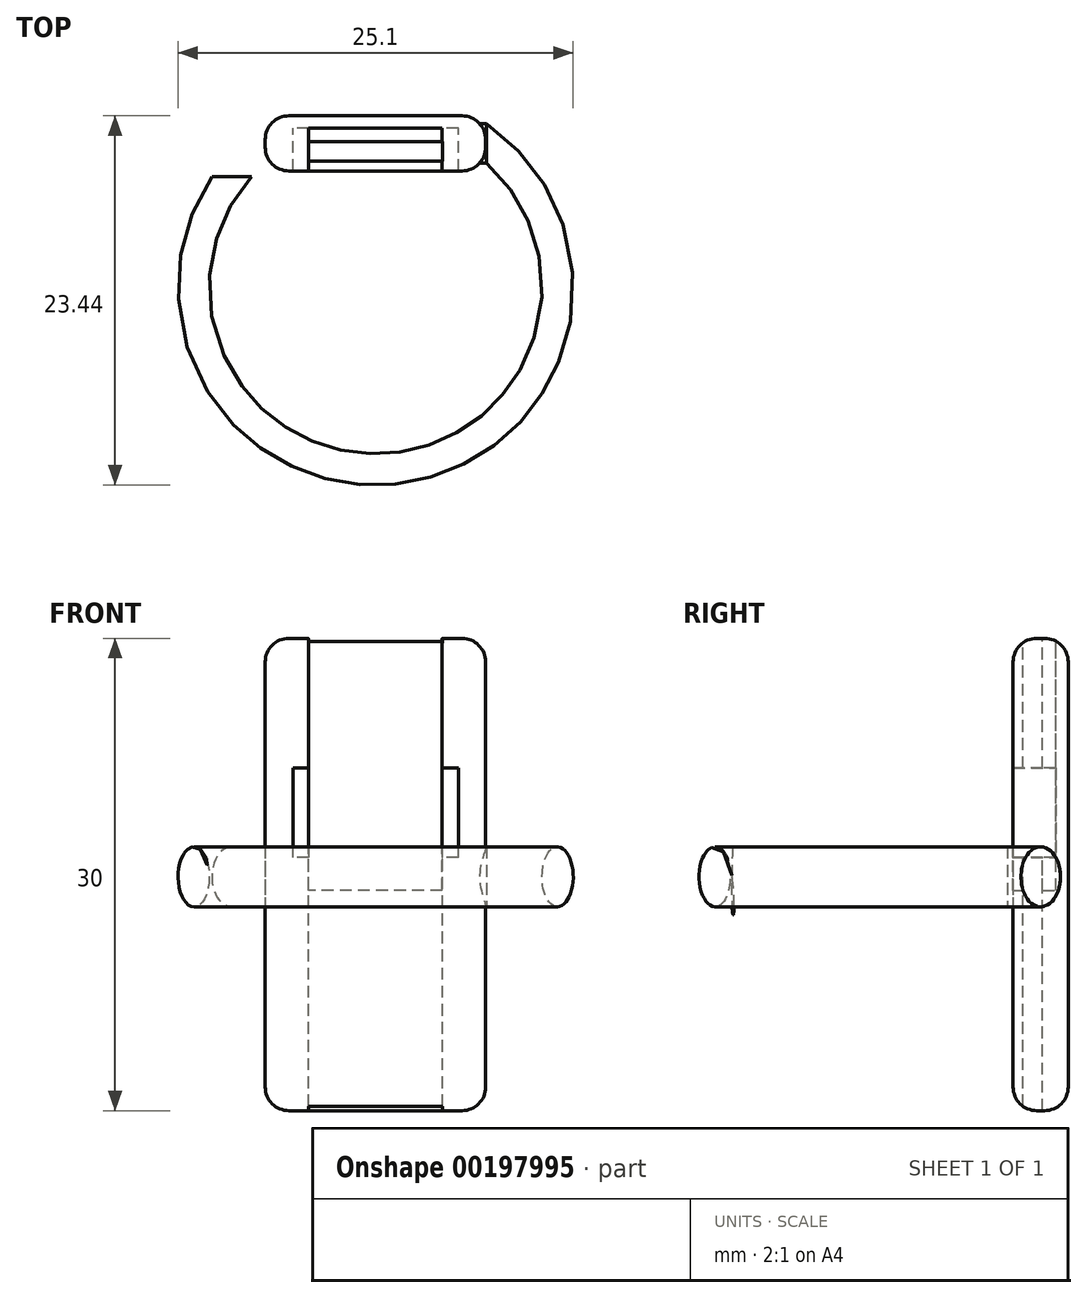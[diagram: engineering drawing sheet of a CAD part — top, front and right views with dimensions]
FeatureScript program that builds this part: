
annotation { "Feature Type Name" : "Feature", "Feature Type Description" : "" }
export const myFeature = defineFeature(function(context is Context, id is Id, definition is map)
    precondition{}
    {
        {
            var Q0;
            Q0=qCreatedBy(makeId("Top.planeOp"),FACE);
            var sketch = newSketch(context, id + "F0", { "sketchPlane" : qUnion([Q0])});
            skLineSegment(sketch, "E0.bottom", {"start": v(7, 1.75) * mm, "end": v(-7, 1.75) * mm});
            skLineSegment(sketch, "E0.top", {"start": v(7, -1.75) * mm, "end": v(-7, -1.75) * mm});
            skLineSegment(sketch, "E0.left", {"start": v(7, 1.75) * mm, "end": v(7, -1.75) * mm});
            skLineSegment(sketch, "E0.right", {"start": v(-7, 1.75) * mm, "end": v(-7, -1.75) * mm});
            skPoint(sketch, "E0.middle", {"position": v(0, 0) * mm});
            skSolve(sketch);
        }
        {
            var Q0;
            Q0=makeQuery(id+"F0.imprint","IMPRINT",FACE,{"disambiguationData":[TD([[makeQuery(id+"F0.imprint","IMPRINT",EDGE,{"derivedFrom":sQuery(id+"F0.wireOp",EDGE,"E0.bottom")}),1.0]])]});
            extrude(context, id + "F1", {"entities" : qUnion([Q0]), "depth" : 30 * mm});
        }
        {
            var Q0;
            Q0=makeQuery(id+"F1.opExtrude","SWEPT_EDGE",EDGE,{"disambiguationData":[OSD([sQuery(id+"F0.wireOp",EDGE,"E0.top"),sQuery(id+"F0.wireOp",EDGE,"E0.right")])]});
            fillet(context, id + "F2", {"entities" : qUnion([Q0]), "radius" : 1.5 * mm, "tangentPropagation" : true, "allowEdgeOverflow" : false});
        }
        {
            var Q0;
            Q0=makeQuery(id+"F1.opExtrude","SWEPT_EDGE",EDGE,{"disambiguationData":[OSD([sQuery(id+"F0.wireOp",EDGE,"E0.bottom"),sQuery(id+"F0.wireOp",EDGE,"E0.right")])]});
            fillet(context, id + "F3", {"entities" : qUnion([Q0]), "radius" : 1.5 * mm, "tangentPropagation" : true, "allowEdgeOverflow" : false});
        }
        {
            var Q0;
            Q0=makeQuery(id+"F1.opExtrude","SWEPT_EDGE",EDGE,{"disambiguationData":[OSD([sQuery(id+"F0.wireOp",EDGE,"E0.top"),sQuery(id+"F0.wireOp",EDGE,"E0.left")])]});
            fillet(context, id + "F4", {"entities" : qUnion([Q0]), "radius" : 1.5 * mm, "tangentPropagation" : true, "allowEdgeOverflow" : false});
        }
        {
            var Q0;
            Q0=makeQuery(id+"F1.opExtrude","SWEPT_EDGE",EDGE,{"disambiguationData":[OSD([sQuery(id+"F0.wireOp",EDGE,"E0.bottom"),sQuery(id+"F0.wireOp",EDGE,"E0.left")])]});
            fillet(context, id + "F5", {"entities" : qUnion([Q0]), "radius" : 1.5 * mm, "tangentPropagation" : true, "allowEdgeOverflow" : false});
        }
        {
            var Q0;
            Q0=makeQuery(id+"F1.opExtrude","CAP_FACE",FACE,{"disambiguationData":[OSD([sQuery(id+"F0.wireOp",EDGE,"E0.bottom"),sQuery(id+"F0.wireOp",EDGE,"E0.top"),sQuery(id+"F0.wireOp",EDGE,"E0.left"),sQuery(id+"F0.wireOp",EDGE,"E0.right")])],"isStart":false});
            var sketch = newSketch(context, id + "F6", { "sketchPlane" : qUnion([Q0])});
            skLineSegment(sketch, "E1.bottom", {"start": v(4.25, -1.12) * mm, "end": v(-4.25, -1.12) * mm});
            skLineSegment(sketch, "E1.top", {"start": v(4.25, 0.13) * mm, "end": v(-4.25, 0.13) * mm});
            skLineSegment(sketch, "E1.left", {"start": v(4.25, -1.12) * mm, "end": v(4.25, 0.13) * mm});
            skLineSegment(sketch, "E1.right", {"start": v(-4.25, -1.12) * mm, "end": v(-4.25, 0.13) * mm});
            skPoint(sketch, "E1.middle", {"position": v(0, -0.5) * mm});
            skSolve(sketch);
        }
        {
            var Q0;
            Q0=makeQuery(id+"F6.imprint","IMPRINT",FACE,{"disambiguationData":[TD([[makeQuery(id+"F6.imprint","IMPRINT",EDGE,{"derivedFrom":sQuery(id+"F6.wireOp",EDGE,"E1.bottom")}),-1.0]])]});
            extrude(context, id + "F7", {"entities" : qUnion([Q0]), "operationType" : NewBodyOperationType.REMOVE, "endBound" : BoundingType.THROUGH_ALL, "oppositeDirection" : true, "depth" : 30 * mm});
        }
        {
            var Q0;
            Q0=makeQuery(id+"F1.opExtrude","CAP_FACE",FACE,{"disambiguationData":[OSD([sQuery(id+"F0.wireOp",EDGE,"E0.bottom"),sQuery(id+"F0.wireOp",EDGE,"E0.top"),sQuery(id+"F0.wireOp",EDGE,"E0.left"),sQuery(id+"F0.wireOp",EDGE,"E0.right")])],"isStart":false});
            var sketch = newSketch(context, id + "F8", { "sketchPlane" : qUnion([Q0])});
            skLineSegment(sketch, "E2.bottom", {"start": v(4.24, -1.75) * mm, "end": v(-4.24, -1.75) * mm});
            skLineSegment(sketch, "E2.top", {"start": v(4.24, 0.97) * mm, "end": v(-4.24, 0.97) * mm});
            skLineSegment(sketch, "E2.left", {"start": v(4.24, -1.75) * mm, "end": v(4.24, 0.97) * mm});
            skLineSegment(sketch, "E2.right", {"start": v(-4.24, -1.75) * mm, "end": v(-4.24, 0.97) * mm});
            skPoint(sketch, "E2.middle", {"position": v(0, -0.39) * mm});
            skPoint(sketch, "E2.middle.positionSnap0", {"position": v(0, -1.12) * mm});
            skPoint(sketch, "E2.centerSnap0", {"position": v(0, -1.12) * mm});
            skSolve(sketch);
        }
        {
            var Q0;
            {var subQ0=sQuery(id+"F8.wireOp",EDGE,"E2.top");Q0=makeQuery(id+"F8.imprint","IMPRINT",FACE,{"disambiguationData":[TD([[makeQuery(id+"F8.imprint","IMPRINT",EDGE,{"derivedFrom":subQ0}),1.0]])]});}
            var Q1;
            {var subQ0=sQuery(id+"F8.wireOp",EDGE,"E2.bottom");Q1=makeQuery(id+"F8.imprint","IMPRINT",FACE,{"disambiguationData":[TD([[makeQuery(id+"F8.imprint","IMPRINT",EDGE,{"derivedFrom":subQ0}),-1.0]])]});}
            extrude(context, id + "F9", {"entities" : qUnion([Q0, Q1]), "operationType" : NewBodyOperationType.REMOVE, "oppositeDirection" : true, "depth" : 16 * mm});
        }
        {
            var Q0;
            {var subQ0=sQuery(id+"F8.wireOp",EDGE,"E2.right");Q0=makeQuery(id+"F9.boolean.opBoolean","COPY",FACE,{"derivedFrom":makeQuery(id+"F9.opExtrude","SWEPT_FACE",FACE,{"disambiguationData":[OSD([subQ0]),TDD([makeQuery(id+"F8.imprint","IMPRINT",EDGE,{"disambiguationData":[TD([[makeQuery(id+"F8.imprint","INTERSECT",VERTEX,{"derivedFrom":[makeQuery(id+"F7.boolean.opBoolean","COPY",EDGE,{"derivedFrom":makeQuery(id+"F7.opExtrude","CAP_EDGE",EDGE,{"disambiguationData":[OSD([sQuery(id+"F6.wireOp",EDGE,"E1.bottom")])],"isStart":true})}),subQ0]}),1.0]])],"derivedFrom":subQ0})])]})});}
            var sketch = newSketch(context, id + "F10", { "sketchPlane" : qUnion([Q0])});
            skLineSegment(sketch, "E3.bottom", {"start": v(-1.75, 16.08) * mm, "end": v(0.96, 16.08) * mm});
            skLineSegment(sketch, "E3.top", {"start": v(-1.75, 21.76) * mm, "end": v(0.96, 21.76) * mm});
            skLineSegment(sketch, "E3.left", {"start": v(-1.75, 16.08) * mm, "end": v(-1.75, 21.76) * mm});
            skLineSegment(sketch, "E3.right", {"start": v(0.96, 16.08) * mm, "end": v(0.96, 21.76) * mm});
            skSolve(sketch);
        }
        {
            var Q0;
            {var subQ0=sQuery(id+"F10.wireOp",EDGE,"E3.right");Q0=makeQuery(id+"F10.imprint","IMPRINT",FACE,{"disambiguationData":[TD([[makeQuery(id+"F10.imprint","IMPRINT",EDGE,{"derivedFrom":subQ0}),1.0]])]});}
            var Q1;
            {var subQ0=sQuery(id+"F10.wireOp",EDGE,"E3.left");Q1=makeQuery(id+"F10.imprint","IMPRINT",FACE,{"disambiguationData":[TD([[makeQuery(id+"F10.imprint","IMPRINT",EDGE,{"derivedFrom":subQ0}),-1.0]])]});}
            extrude(context, id + "F11", {"entities" : qUnion([Q0, Q1]), "operationType" : NewBodyOperationType.REMOVE, "depth" : 9.5 * mm, "hasSecondDirection" : true, "secondDirectionOppositeDirection" : true, "secondDirectionDepth" : 1 * mm});
        }
        {
            var Q0;
            Q0=qCreatedBy(makeId("Top.planeOp"),FACE);
            var sketch = newSketch(context, id + "F12", { "sketchPlane" : qUnion([Q0])});
            skCircle(sketch, "E4", {"center": v(0.01, -9.15) * mm, "radius": 10.5 * mm});
            skPoint(sketch, "E4.first.point", {"position": v(-6.92, -1.26) * mm});
            skPoint(sketch, "E4.second.point", {"position": v(6.87, -1.2) * mm});
            skPoint(sketch, "E4.third.point", {"position": v(7.13, -16.86) * mm});
            skSolve(sketch);
        }
        {
            var Q0;
            Q0=makeQuery(id+"F11.boolean.opBoolean","COPY",FACE,{"derivedFrom":makeQuery(id+"F11.opExtrude","CAP_FACE",FACE,{"disambiguationData":[OSD([sQuery(id+"F10.wireOp",EDGE,"E3.bottom"),sQuery(id+"F10.wireOp",EDGE,"E3.top"),sQuery(id+"F10.wireOp",EDGE,"E3.left"),sQuery(id+"F10.wireOp",EDGE,"E3.right")])],"isStart":false})});
            var sketch = newSketch(context, id + "F13", { "sketchPlane" : qUnion([Q0])});
            skEllipse(sketch, "E5", {"center": v(0, 14.86) * mm, "majorRadius": 1.9 * mm, "minorRadius": 1.25 * mm, "majorAxis": v(0, 1)});
            skSolve(sketch);
        }
        {
            var Q0;
            Q0=makeQuery(id+"F1.opExtrude","CAP_EDGE",EDGE,{"disambiguationData":[OSD([sQuery(id+"F0.wireOp",EDGE,"E0.bottom")])],"isStart":false});
            fillet(context, id + "F14", {"entities" : qUnion([Q0]), "radius" : 1.5 * mm, "tangentPropagation" : true, "allowEdgeOverflow" : false});
        }
        {
            var Q0;
            Q0=makeQuery(id+"F1.opExtrude","CAP_EDGE",EDGE,{"disambiguationData":[OSD([sQuery(id+"F0.wireOp",EDGE,"E0.top")])],"isStart":true});
            fillet(context, id + "F15", {"entities" : qUnion([Q0]), "radius" : 1.5 * mm, "tangentPropagation" : true, "allowEdgeOverflow" : false});
        }
        {
            var Q0;
            Q0 = qSketchRegion(id + "F13", true);
            extrude(context, id + "F16", {"entities" : qUnion([Q0]), "operationType" : NewBodyOperationType.ADD, "oppositeDirection" : true, "depth" : 1.78 * mm});
        }
        {
            var Q0;
            Q0=makeQuery(id+"F16.opExtrude","CAP_FACE",FACE,{"disambiguationData":[OSD([sQuery(id+"F13.wireOp",EDGE,"E5")])],"isStart":false});
            var Q1;
            Q1=sQuery(id+"F12.wireOp",EDGE,"E4");
            revolve(context, id + "F17", {"operationType" : NewBodyOperationType.ADD, "entities" : qUnion([Q0]), "axis" : qUnion([Q1]), "revolveType" : RevolveType.ONE_DIRECTION, "oppositeDirection" : true, "angle" : 270 * degree});
        }
    });
